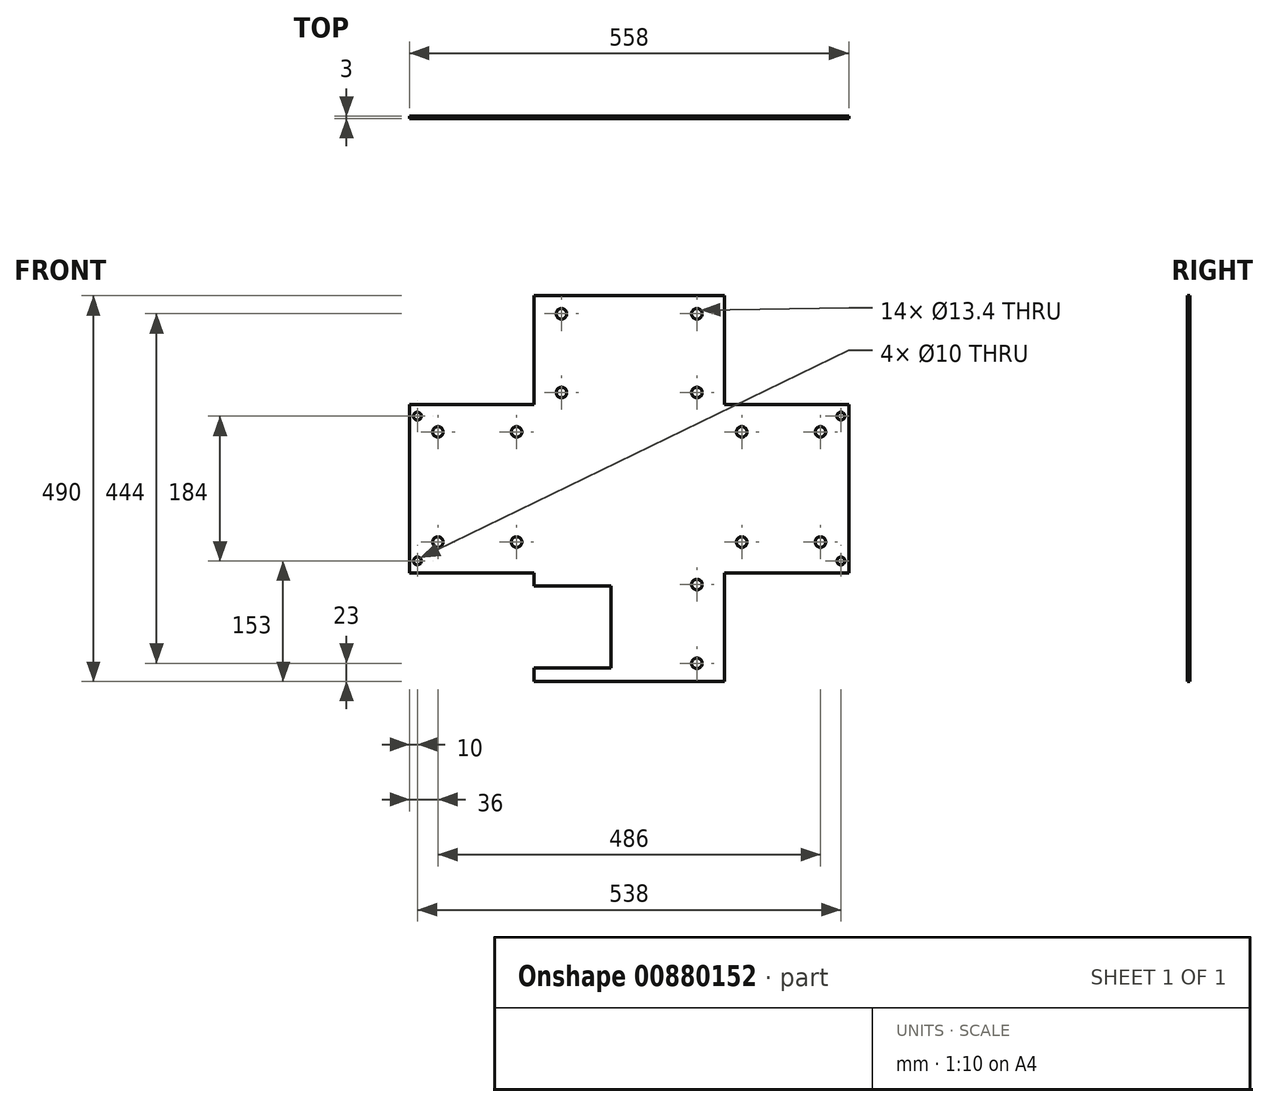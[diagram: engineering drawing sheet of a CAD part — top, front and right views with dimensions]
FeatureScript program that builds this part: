
annotation { "Feature Type Name" : "Feature", "Feature Type Description" : "" }
export const myFeature = defineFeature(function(context is Context, id is Id, definition is map)
    precondition{}
    {
        {
            var Q0;
            Q0=qCreatedBy(makeId("Front.planeOp"),FACE);
            var sketch = newSketch(context, id + "F0", { "sketchPlane" : qUnion([Q0])});
            skLineSegment(sketch, "E0", {"start": v(0, 0) * mm, "end": v(-242, 0) * mm});
            skLineSegment(sketch, "E1", {"start": v(-242, 0) * mm, "end": v(-242, -138) * mm});
            skLineSegment(sketch, "E2", {"start": v(-242, -138) * mm, "end": v(0, -138) * mm});
            skLineSegment(sketch, "E3", {"start": v(0, -138) * mm, "end": v(0, 0) * mm});
            skLineSegment(sketch, "E4", {"start": v(-242, -352) * mm, "end": v(-242, -138) * mm});
            skLineSegment(sketch, "E5", {"start": v(-242, -352) * mm, "end": v(0, -352) * mm});
            skLineSegment(sketch, "E6", {"start": v(0, -352) * mm, "end": v(0, -138) * mm});
            skLineSegment(sketch, "E7", {"start": v(-242, -352) * mm, "end": v(-242, -369) * mm});
            skLineSegment(sketch, "E8", {"start": v(-242, -369) * mm, "end": v(-144, -369) * mm});
            skLineSegment(sketch, "E9", {"start": v(0, -352) * mm, "end": v(0, -490) * mm});
            skLineSegment(sketch, "E10", {"start": v(0, -490) * mm, "end": v(-144, -490) * mm});
            skLineSegment(sketch, "E11", {"start": v(-144, -490) * mm, "end": v(-242, -490) * mm});
            skLineSegment(sketch, "E12", {"start": v(-242, -490) * mm, "end": v(-242, -473) * mm});
            skLineSegment(sketch, "E13", {"start": v(-242, -473) * mm, "end": v(-144, -473) * mm});
            skLineSegment(sketch, "E14", {"start": v(-144, -473) * mm, "end": v(-144, -369) * mm});
            skLineSegment(sketch, "E15", {"start": v(-242, -138) * mm, "end": v(-380, -138) * mm});
            skLineSegment(sketch, "E16", {"start": v(-380, -138) * mm, "end": v(-380, -352) * mm});
            skLineSegment(sketch, "E17", {"start": v(-380, -352) * mm, "end": v(-242, -352) * mm});
            skLineSegment(sketch, "E18", {"start": v(-380, -352) * mm, "end": v(-400, -352) * mm});
            skLineSegment(sketch, "E19", {"start": v(-400, -352) * mm, "end": v(-400, -138) * mm});
            skLineSegment(sketch, "E20", {"start": v(-400, -138) * mm, "end": v(-380, -138) * mm});
            skLineSegment(sketch, "E21", {"start": v(0, -138) * mm, "end": v(138, -138) * mm});
            skLineSegment(sketch, "E22", {"start": v(138, -138) * mm, "end": v(138, -352) * mm});
            skLineSegment(sketch, "E23", {"start": v(138, -352) * mm, "end": v(0, -352) * mm});
            skLineSegment(sketch, "E24", {"start": v(138, -352) * mm, "end": v(158, -352) * mm});
            skLineSegment(sketch, "E25", {"start": v(158, -352) * mm, "end": v(158, -138) * mm});
            skLineSegment(sketch, "E26", {"start": v(158, -138) * mm, "end": v(138, -138) * mm});
            skLineSegment(sketch, "E27", {"start": v(148, -352) * mm, "end": v(148, -337) * mm});
            skCircle(sketch, "E28", {"center": v(148, -337) * mm, "radius": 5 * mm});
            skLineSegment(sketch, "E29", {"start": v(148, -138) * mm, "end": v(148, -153) * mm});
            skCircle(sketch, "E30", {"center": v(148, -153) * mm, "radius": 5 * mm});
            skLineSegment(sketch, "E31", {"start": v(-390, -138) * mm, "end": v(-390, -153) * mm});
            skCircle(sketch, "E32", {"center": v(-390, -153) * mm, "radius": 5 * mm});
            skLineSegment(sketch, "E33", {"start": v(-390, -352) * mm, "end": v(-390, -337) * mm});
            skCircle(sketch, "E34", {"center": v(-390, -337) * mm, "radius": 5 * mm});
            skLineSegment(sketch, "E35", {"start": v(-121, 0) * mm, "end": v(-121, -23) * mm});
            skLineSegment(sketch, "E36", {"start": v(-121, -23) * mm, "end": v(-207, -23) * mm});
            skLineSegment(sketch, "E37", {"start": v(-207, -23) * mm, "end": v(-35, -23) * mm});
            skLineSegment(sketch, "E38", {"start": v(-207, -23) * mm, "end": v(-207, -123) * mm});
            skLineSegment(sketch, "E39", {"start": v(-207, -123) * mm, "end": v(-35, -123) * mm});
            skCircle(sketch, "E40", {"center": v(-207, -23) * mm, "radius": 6.7 * mm});
            skCircle(sketch, "E41", {"center": v(-35, -23) * mm, "radius": 6.7 * mm});
            skCircle(sketch, "E42", {"center": v(-207, -123) * mm, "radius": 6.7 * mm});
            skCircle(sketch, "E43", {"center": v(-35, -123) * mm, "radius": 6.7 * mm});
            skLineSegment(sketch, "E44", {"start": v(-242, -490) * mm, "end": v(-121, -490) * mm});
            skLineSegment(sketch, "E45", {"start": v(-121, -490) * mm, "end": v(-121, -467) * mm});
            skLineSegment(sketch, "E46", {"start": v(-121, -467) * mm, "end": v(-35, -467) * mm});
            skLineSegment(sketch, "E47", {"start": v(-35, -467) * mm, "end": v(-35, -367) * mm});
            skCircle(sketch, "E48", {"center": v(-35, -367) * mm, "radius": 6.7 * mm});
            skCircle(sketch, "E49", {"center": v(-35, -467) * mm, "radius": 6.7 * mm});
            skLineSegment(sketch, "E50", {"start": v(0, -138) * mm, "end": v(22, -138) * mm});
            skLineSegment(sketch, "E51", {"start": v(22, -138) * mm, "end": v(22, -173) * mm});
            skLineSegment(sketch, "E52", {"start": v(22, -173) * mm, "end": v(122, -173) * mm});
            skLineSegment(sketch, "E53", {"start": v(122, -173) * mm, "end": v(122, -313) * mm});
            skLineSegment(sketch, "E54", {"start": v(122, -313) * mm, "end": v(22, -313) * mm});
            skCircle(sketch, "E55", {"center": v(22, -173) * mm, "radius": 6.7 * mm});
            skCircle(sketch, "E56", {"center": v(22, -313) * mm, "radius": 6.7 * mm});
            skCircle(sketch, "E57", {"center": v(122, -313) * mm, "radius": 6.7 * mm});
            skCircle(sketch, "E58", {"center": v(122, -173) * mm, "radius": 6.7 * mm});
            skLineSegment(sketch, "E59", {"start": v(-242, -138) * mm, "end": v(-264, -138) * mm});
            skLineSegment(sketch, "E60", {"start": v(-264, -138) * mm, "end": v(-264, -173) * mm});
            skLineSegment(sketch, "E61", {"start": v(-264, -173) * mm, "end": v(-364, -173) * mm});
            skLineSegment(sketch, "E62", {"start": v(-364, -173) * mm, "end": v(-364, -313) * mm});
            skLineSegment(sketch, "E63", {"start": v(-364, -313) * mm, "end": v(-264, -313) * mm});
            skCircle(sketch, "E64", {"center": v(-264, -313) * mm, "radius": 6.7 * mm});
            skCircle(sketch, "E65", {"center": v(-364, -313) * mm, "radius": 6.7 * mm});
            skCircle(sketch, "E66", {"center": v(-364, -173) * mm, "radius": 6.7 * mm});
            skCircle(sketch, "E67", {"center": v(-264, -173) * mm, "radius": 6.7 * mm});
            skSolve(sketch);
        }
        {
            var Q0;
            Q0 = qSketchRegion(id + "F0", true);
            extrude(context, id + "F1", {"entities" : qUnion([Q0]), "depth" : 3 * mm, "offsetDistance" : 25 * mm});
        }
    });
